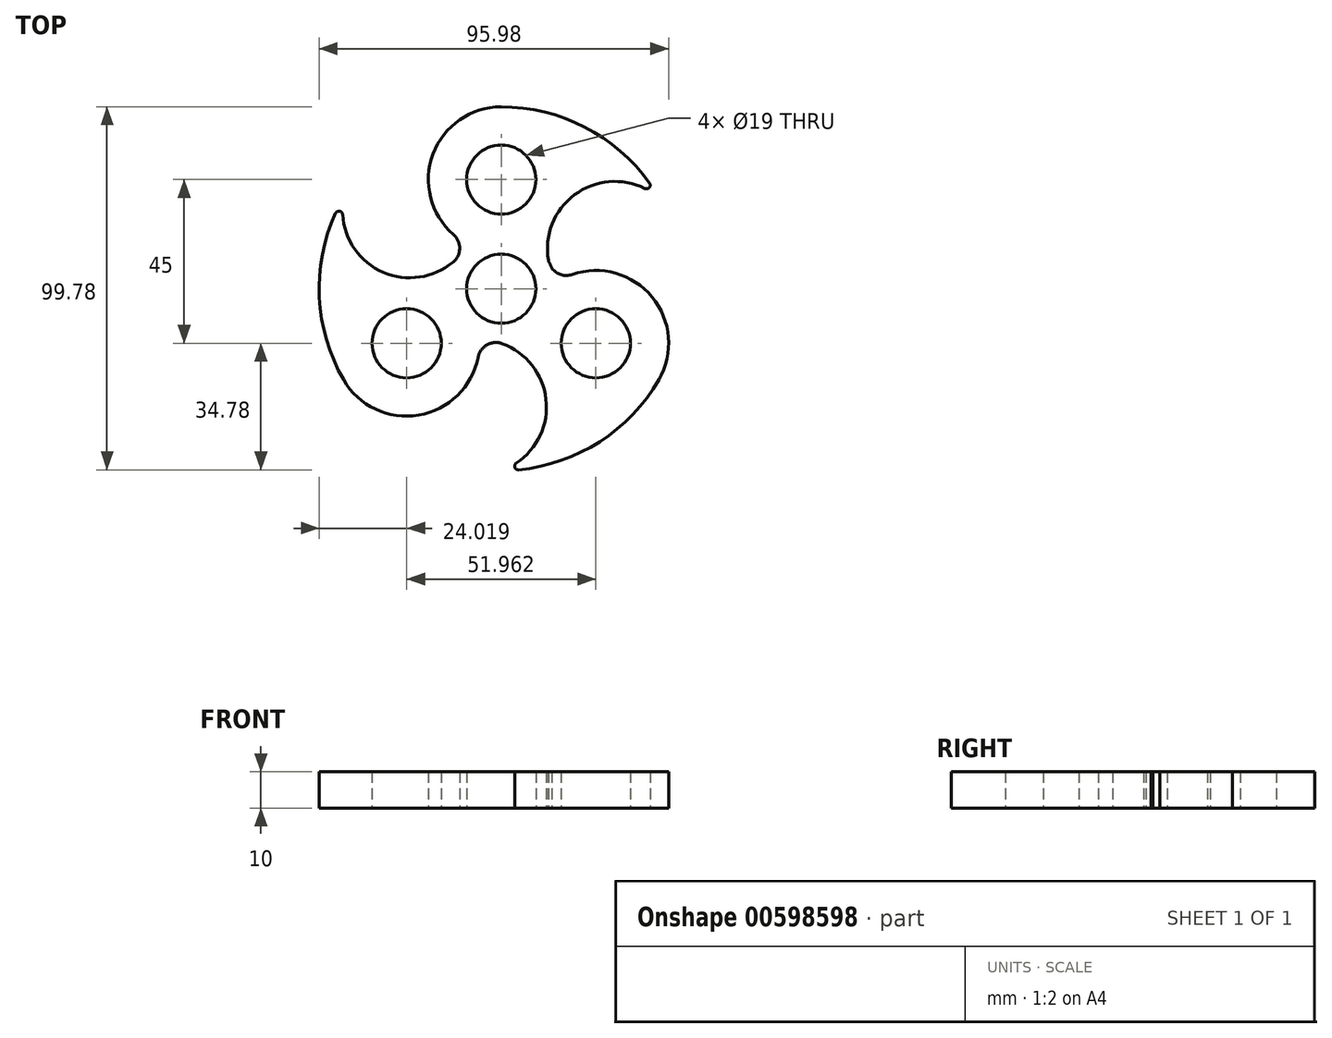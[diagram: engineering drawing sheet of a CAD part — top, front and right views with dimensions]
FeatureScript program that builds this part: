
annotation { "Feature Type Name" : "Feature", "Feature Type Description" : "" }
export const myFeature = defineFeature(function(context is Context, id is Id, definition is map)
    precondition{}
    {
        {
            var Q0;
            Q0=qCreatedBy(makeId("Top.planeOp"),FACE);
            var sketch = newSketch(context, id + "F0", { "sketchPlane" : qUnion([Q0])});
            skArc(sketch, "E0", {"start": v(4.78, -49.77) * mm, "mid": v(27.04, -42.05) * mm, "end": v(43.3, -25) * mm});
            skCircle(sketch, "E1", {"center": v(0, 0) * mm, "radius": 9.5 * mm});
            skCircle(sketch, "E2", {"center": v(0, 30) * mm, "radius": 9.5 * mm});
            skCircle(sketch, "E3.1.0", {"center": v(-25.98, -15) * mm, "radius": 9.5 * mm});
            skCircle(sketch, "E3.2.0", {"center": v(25.98, -15) * mm, "radius": 9.5 * mm});
            skArc(sketch, "E4", {"start": v(-12.98, 7.52) * mm, "mid": v(-12.98, 7.51) * mm, "end": v(-13, 7.5) * mm});
            skArc(sketch, "E5", {"start": v(39.45, 27.55) * mm, "mid": v(20.14, 25.81) * mm, "end": v(12.94, 7.8) * mm});
            skArc(sketch, "E6.1.0", {"start": v(-43.59, 20.4) * mm, "mid": v(-32.42, 4.53) * mm, "end": v(-13.22, 7.3) * mm});
            skPoint(sketch, "E7.orphan", {"position": v(43.3, 25) * mm});
            skArc(sketch, "E8.trimOffspring", {"start": v(4.13, -47.94) * mm, "mid": v(12.28, -30.34) * mm, "end": v(0.29, -15.1) * mm});
            skArc(sketch, "E9", {"start": v(43.3, -25) * mm, "mid": v(41.42, -2.29) * mm, "end": v(19.49, 3.92) * mm});
            skArc(sketch, "E10.1.0", {"start": v(0, 50) * mm, "mid": v(-18.73, 37.01) * mm, "end": v(-13.14, 14.92) * mm});
            skArc(sketch, "E10.2.0", {"start": v(-43.3, -25) * mm, "mid": v(-22.69, -34.73) * mm, "end": v(-6.35, -18.84) * mm});
            skArc(sketch, "E11.filletArc", {"start": v(-13.22, 7.3) * mm, "mid": v(-11.42, 11.1) * mm, "end": v(-13.14, 14.92) * mm});
            skArc(sketch, "E12.filletArc", {"start": v(12.94, 7.8) * mm, "mid": v(15.31, 4.34) * mm, "end": v(19.49, 3.92) * mm});
            skArc(sketch, "E13.filletArc", {"start": v(0.29, -15.1) * mm, "mid": v(-3.9, -15.44) * mm, "end": v(-6.35, -18.84) * mm});
            skArc(sketch, "E14.trimOffspring", {"start": v(40.71, 29.03) * mm, "mid": v(22.9, 44.45) * mm, "end": v(0, 50) * mm});
            skArc(sketch, "E15.trimOffspring", {"start": v(-45.5, 20.74) * mm, "mid": v(-49.94, -2.4) * mm, "end": v(-43.3, -25) * mm});
            skArc(sketch, "E16.filletArc", {"start": v(39.45, 27.55) * mm, "mid": v(40.66, 27.8) * mm, "end": v(40.71, 29.03) * mm});
            skLineSegment(sketch, "E17.trimOffspring", {"start": v(-13, 7.5) * mm, "end": v(-13, 7.5) * mm});
            skArc(sketch, "E18.filletArc", {"start": v(-43.59, 20.4) * mm, "mid": v(-44.4, 21.31) * mm, "end": v(-45.5, 20.74) * mm});
            skLineSegment(sketch, "E19.trimOffspring", {"start": v(0, -15) * mm, "end": v(0, -15) * mm});
            skPoint(sketch, "E20.visualSharp", {"position": v(0, -50) * mm});
            skArc(sketch, "E20.filletArc", {"start": v(4.13, -47.94) * mm, "mid": v(3.74, -49.11) * mm, "end": v(4.78, -49.77) * mm});
            skArc(sketch, "E21.trimOffspring", {"start": v(-0.02, -15) * mm, "mid": v(-0.01, -15) * mm, "end": v(0, -15) * mm});
            skArc(sketch, "E22.trimOffspring", {"start": v(13.93, 5.56) * mm, "mid": v(13.5, 6.53) * mm, "end": v(13, 7.48) * mm});
            skSolve(sketch);
        }
        {
            var Q0;
            Q0=qSketchRegion(id+"F0",true);
            extrude(context, id + "F1", {"entities" : qUnion([Q0]), "depth" : 10 * mm, "offsetDistance" : 25 * mm});
        }
    });
